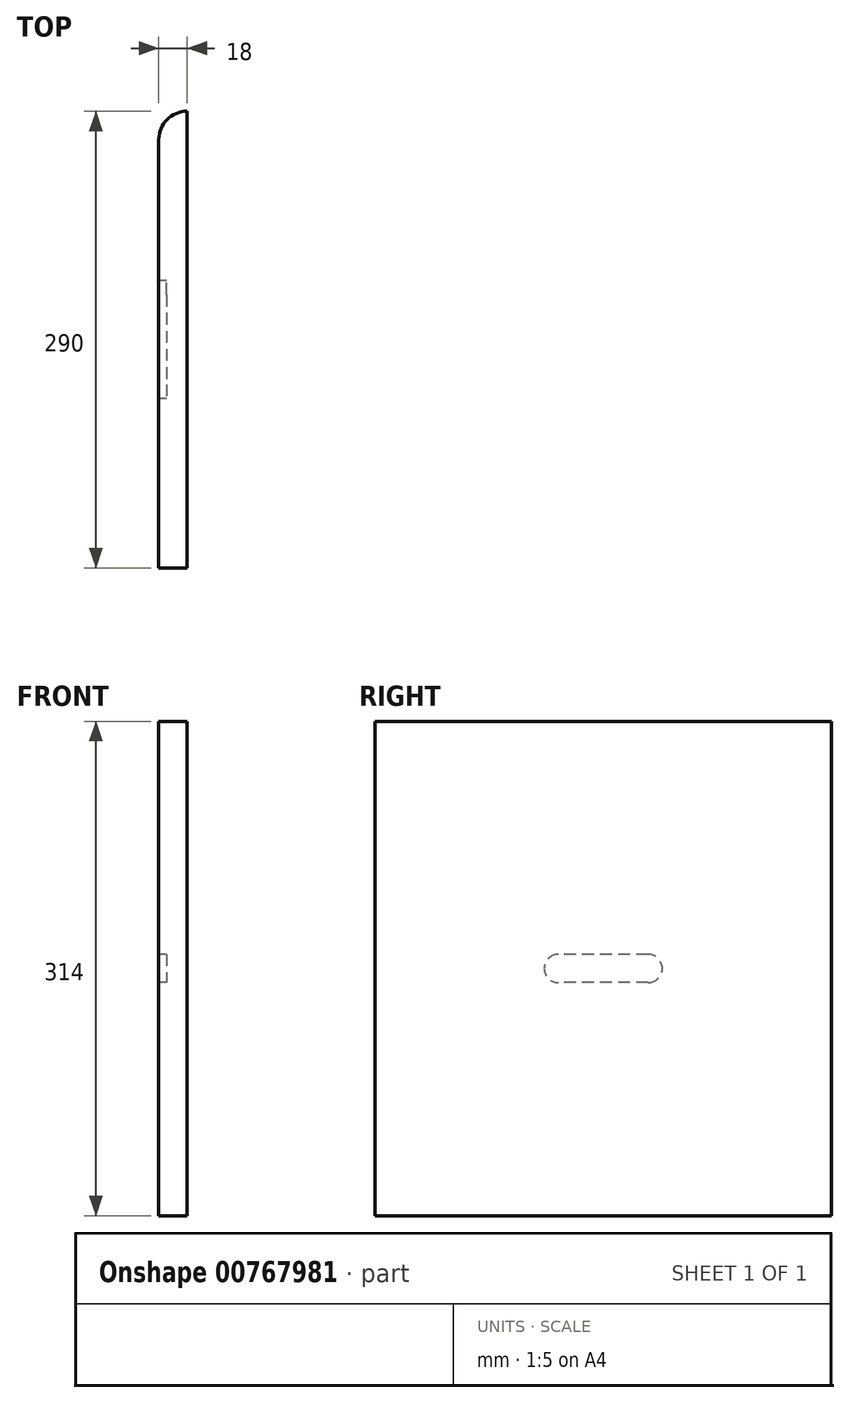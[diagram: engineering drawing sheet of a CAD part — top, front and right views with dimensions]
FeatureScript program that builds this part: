
annotation { "Feature Type Name" : "Feature", "Feature Type Description" : "" }
export const myFeature = defineFeature(function(context is Context, id is Id, definition is map)
    precondition{}
    {
        {
            var Q0;
            Q0=qCreatedBy(makeId("Right.planeOp"),FACE);
            var sketch = newSketch(context, id + "F0", { "sketchPlane" : qUnion([Q0])});
            skLineSegment(sketch, "E0.bottom", {"start": v(-145, 157) * mm, "end": v(145, 157) * mm});
            skLineSegment(sketch, "E0.top", {"start": v(-145, -157) * mm, "end": v(145, -157) * mm});
            skLineSegment(sketch, "E0.left", {"start": v(-145, 157) * mm, "end": v(-145, -157) * mm});
            skLineSegment(sketch, "E0.right", {"start": v(145, 157) * mm, "end": v(145, -157) * mm});
            skPoint(sketch, "E0.middle", {"position": v(0, 0) * mm});
            skSolve(sketch);
        }
        {
            var Q0;
            Q0 = qSketchRegion(id + "F0", true);
            extrude(context, id + "F1", {"entities" : qUnion([Q0]), "depth" : 18 * mm, "offsetDistance" : 25 * mm});
        }
        {
            var Q0;
            Q0=makeQuery(id+"F1.opExtrude","CAP_FACE",FACE,{"disambiguationData":[OSD([sQuery(id+"F0.wireOp",EDGE,"E0.bottom"),sQuery(id+"F0.wireOp",EDGE,"E0.top"),sQuery(id+"F0.wireOp",EDGE,"E0.left"),sQuery(id+"F0.wireOp",EDGE,"E0.right")])],"isStart":true});
            var sketch = newSketch(context, id + "F2", { "sketchPlane" : qUnion([Q0])});
            skLineSegment(sketch, "E1.bottom", {"start": v(-28.5, 9) * mm, "end": v(28.5, 9) * mm});
            skLineSegment(sketch, "E1.top", {"start": v(-28.5, -9) * mm, "end": v(28.5, -9) * mm});
            skLineSegment(sketch, "E1.left", {"start": v(-28.5, 9) * mm, "end": v(-28.5, -9) * mm, "construction": true});
            skLineSegment(sketch, "E1.right", {"start": v(28.5, 9) * mm, "end": v(28.5, -9) * mm, "construction": true});
            skPoint(sketch, "E1.middle", {"position": v(0, 0) * mm});
            skArc(sketch, "E2", {"start": v(-28.5, 9) * mm, "mid": v(-37.5, 0) * mm, "end": v(-28.5, -9) * mm});
            skArc(sketch, "E3", {"start": v(28.5, 9) * mm, "mid": v(37.5, 0) * mm, "end": v(28.5, -9) * mm});
            skSolve(sketch);
        }
        {
            var Q0;
            Q0 = qSketchRegion(id + "F2", true);
            extrude(context, id + "F3", {"entities" : qUnion([Q0]), "operationType" : NewBodyOperationType.REMOVE, "oppositeDirection" : true, "depth" : 5 * mm, "offsetDistance" : 25 * mm});
        }
        {
            var Q0;
            Q0=makeQuery(id+"F1.opExtrude","CAP_EDGE",EDGE,{"disambiguationData":[OSD([sQuery(id+"F0.wireOp",EDGE,"E0.right")])],"isStart":true});
            fillet(context, id + "F4", {"entities" : qUnion([Q0]), "radius" : 18 * mm, "tangentPropagation" : true, "allowEdgeOverflow" : false});
        }
    });
